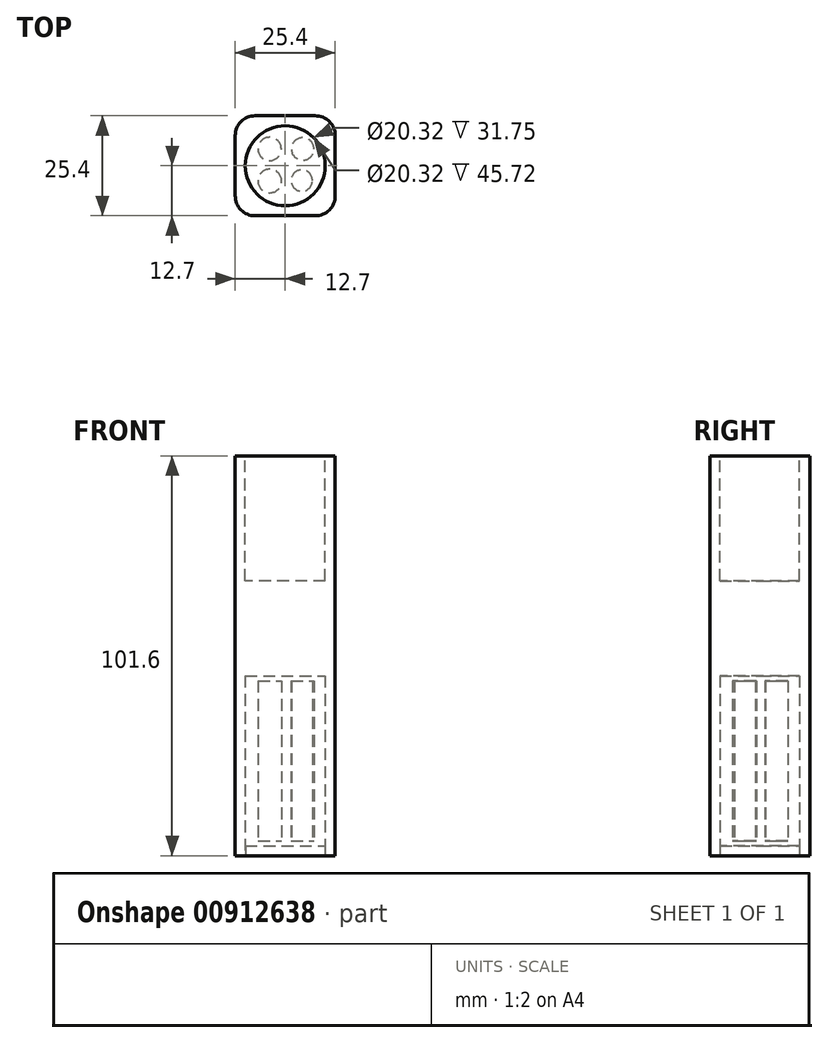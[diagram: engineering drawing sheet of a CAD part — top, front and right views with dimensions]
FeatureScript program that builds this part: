
annotation { "Feature Type Name" : "Feature", "Feature Type Description" : "" }
export const myFeature = defineFeature(function(context is Context, id is Id, definition is map)
    precondition{}
    {
        {
            var Q0;
            Q0=qCreatedBy(makeId("Front.planeOp"),FACE);
            var sketch = newSketch(context, id + "F0", { "sketchPlane" : qUnion([Q0])});
            skLineSegment(sketch, "E0", {"start": v(-12.7, 66.78) * mm, "end": v(-12.7, -34.82) * mm});
            skLineSegment(sketch, "E1.MirrorCS", {"start": v(12.7, 66.78) * mm, "end": v(12.7, -34.82) * mm});
            skLineSegment(sketch, "E2", {"start": v(-12.7, -34.82) * mm, "end": v(12.7, -34.82) * mm});
            skLineSegment(sketch, "E3", {"start": v(-12.7, 66.78) * mm, "end": v(12.7, 66.78) * mm});
            skPoint(sketch, "E4.visualSharp", {"position": v(-12.7, 66.78) * mm});
            skSolve(sketch);
        }
        {
            var Q0;
            Q0=makeQuery(id+"F0.imprint","IMPRINT",FACE,{"disambiguationData":[TD([[makeQuery(id+"F0.imprint","IMPRINT",EDGE,{"derivedFrom":sQuery(id+"F0.wireOp",EDGE,"E0")}),1.0]])]});
            extrude(context, id + "F1", {"entities" : qUnion([Q0]), "endBound" : BoundingType.SYMMETRIC, "depth" : 25.4 * mm, "offsetDistance" : 25.4 * mm});
        }
        {
            var Q0;
            Q0=makeQuery(id+"F1.opExtrude","CAP_EDGE",EDGE,{"disambiguationData":[OSD([sQuery(id+"F0.wireOp",EDGE,"E0")])],"isStart":true});
            var Q1;
            Q1=makeQuery(id+"F1.opExtrude","CAP_EDGE",EDGE,{"disambiguationData":[OSD([sQuery(id+"F0.wireOp",EDGE,"E0")])],"isStart":false});
            var Q2;
            Q2=makeQuery(id+"F1.opExtrude","CAP_EDGE",EDGE,{"disambiguationData":[OSD([sQuery(id+"F0.wireOp",EDGE,"E1.MirrorCS")])],"isStart":true});
            var Q3;
            Q3=makeQuery(id+"F1.opExtrude","CAP_EDGE",EDGE,{"disambiguationData":[OSD([sQuery(id+"F0.wireOp",EDGE,"E1.MirrorCS")])],"isStart":false});
            fillet(context, id + "F2", {"entities" : qUnion([Q0, Q1, Q2, Q3]), "radius" : 5.08 * mm, "tangentPropagation" : true, "allowEdgeOverflow" : false});
        }
        {
            var Q0;
            Q0=makeQuery(id+"F1.opExtrude","SWEPT_FACE",FACE,{"disambiguationData":[OSD([sQuery(id+"F0.wireOp",EDGE,"E3")])]});
            var sketch = newSketch(context, id + "F3", { "sketchPlane" : qUnion([Q0])});
            skCircle(sketch, "E5", {"center": v(0, 0) * mm, "radius": 10.16 * mm});
            skSolve(sketch);
        }
        {
            var Q0;
            Q0 = qSketchRegion(id + "F3", true);
            extrude(context, id + "F4", {"entities" : qUnion([Q0]), "operationType" : NewBodyOperationType.REMOVE, "oppositeDirection" : true, "depth" : 31.75 * mm, "offsetDistance" : 25.4 * mm});
        }
        {
            var Q0;
            Q0=makeQuery(id+"F1.opExtrude","SWEPT_FACE",FACE,{"disambiguationData":[OSD([sQuery(id+"F0.wireOp",EDGE,"E2")])]});
            var sketch = newSketch(context, id + "F5", { "sketchPlane" : qUnion([Q0])});
            skCircle(sketch, "E6", {"center": v(0, 0) * mm, "radius": 10.16 * mm});
            skSolve(sketch);
        }
        {
            var Q0;
            Q0=makeQuery(id+"F5.imprint","IMPRINT",FACE,{"disambiguationData":[TD([[makeQuery(id+"F5.imprint","IMPRINT",EDGE,{"derivedFrom":sQuery(id+"F5.wireOp",EDGE,"E6")}),1.0]])]});
            extrude(context, id + "F6", {"entities" : qUnion([Q0]), "operationType" : NewBodyOperationType.REMOVE, "oppositeDirection" : true, "depth" : 45.72 * mm, "offsetDistance" : 25.4 * mm});
        }
        {
            var Q0;
            Q0=makeQuery(id+"F1.opExtrude","SWEPT_FACE",FACE,{"disambiguationData":[OSD([sQuery(id+"F0.wireOp",EDGE,"E2")])]});
            var sketch = newSketch(context, id + "F7", { "sketchPlane" : qUnion([Q0])});
            skCircle(sketch, "E7", {"center": v(-3.94, 3.87) * mm, "radius": 3 * mm});
            skCircle(sketch, "E8", {"center": v(-3.94, -4.27) * mm, "radius": 2.96 * mm});
            skCircle(sketch, "E9", {"center": v(4.2, 3.76) * mm, "radius": 2.71 * mm});
            skCircle(sketch, "E10", {"center": v(4.44, -4.27) * mm, "radius": 2.87 * mm});
            skSolve(sketch);
        }
        {
            var Q0;
            Q0=makeQuery(id+"F7.imprint","IMPRINT",FACE,{"disambiguationData":[TD([[makeQuery(id+"F7.imprint","IMPRINT",EDGE,{"derivedFrom":sQuery(id+"F7.wireOp",EDGE,"E7")}),1.0]])]});
            var Q1;
            Q1=makeQuery(id+"F7.imprint","IMPRINT",FACE,{"disambiguationData":[TD([[makeQuery(id+"F7.imprint","IMPRINT",EDGE,{"derivedFrom":sQuery(id+"F7.wireOp",EDGE,"E9")}),1.0]])]});
            var Q2;
            Q2=makeQuery(id+"F7.imprint","IMPRINT",FACE,{"disambiguationData":[TD([[makeQuery(id+"F7.imprint","IMPRINT",EDGE,{"derivedFrom":sQuery(id+"F7.wireOp",EDGE,"E8")}),1.0]])]});
            var Q3;
            Q3=makeQuery(id+"F7.imprint","IMPRINT",FACE,{"disambiguationData":[TD([[makeQuery(id+"F7.imprint","IMPRINT",EDGE,{"derivedFrom":sQuery(id+"F7.wireOp",EDGE,"E10")}),1.0]])]});
            extrude(context, id + "F8", {"entities" : qUnion([Q0, Q1, Q2, Q3]), "oppositeDirection" : true, "depth" : 44.45 * mm, "offsetDistance" : 25.4 * mm, "hasSecondDirection" : true, "secondDirectionOppositeDirection" : true, "secondDirectionDepth" : 3.8 * mm});
        }
        {
            var Q0;
            Q0=makeQuery(id+"F1.opExtrude","SWEPT_FACE",FACE,{"disambiguationData":[OSD([sQuery(id+"F0.wireOp",EDGE,"E2")])]});
            var sketch = newSketch(context, id + "F9", { "sketchPlane" : qUnion([Q0])});
            skCircle(sketch, "E11", {"center": v(0, 0) * mm, "radius": 10.1 * mm});
            skSolve(sketch);
        }
        {
            var Q0;
            Q0=makeQuery(id+"F9.imprint","IMPRINT",FACE,{"disambiguationData":[TD([[makeQuery(id+"F9.imprint","IMPRINT",EDGE,{"derivedFrom":sQuery(id+"F9.wireOp",EDGE,"E11")}),1.0]])]});
            extrude(context, id + "F10", {"entities" : qUnion([Q0]), "oppositeDirection" : true, "depth" : 2.54 * mm, "offsetDistance" : 25.4 * mm});
        }
    });
